# Revit family: Faucet-Two_Handle-American_Standard-Monterrey-6409180.002
name_source: partatom
category: Plumbing Fixtures
units: mm (PartAtom-declared; Revit-internal decimal feet)

## family parameters
Always vertical = No
Cut with Voids When Loaded = No
OmniClass Number = 23.45.55.17
OmniClass Title = Mixing Faucets
Part Type = Normal
Room Calculation Point = No
Round Connector Dimension = Use Diameter
Shared = Yes
Work Plane-Based = Yes

## types (1)
- 6409180.002
    ADA Compliant = Yes
    Assembly Code = D2020300
    CW Connection = Yes
    CWFU = 1.5
    CalGreen Compliant = Yes
    Cold Water Connection Diameter = 1/2"
    Compliance Certifications = These products meet or exceed the following codes and standards: ASME A112.18.1, CSA B125.1
NSF 61/Section 9, Annex G
CALGreen
    Default Elevation = 0"
    Description = Monterrey® Top Mount Kitchen Faucet With Gooseneck Spout and Wrist Blade Handles 1.5 gpm/5.7 Lpf Laminar Flow in Spout Base
    Finish = Brass-American Standard-002-Polished Chrome
    Flow Rate = 1.5gpm (5.7L/min)
    HW Connection = Yes
    HWFU = 1.5
    Height = 13 3/8"
    Hot Water Connection Diameter = 1/2"
    Installation Type = Deck Mounted
    L10 1.0 gpm (3.8 Lpm) PCA Non-Aerated Laminar Flow Outlet = No
    Length = 8"
    Manufacturer = American Standard
    Material = Brass-American Standard-002-Polished Chrome
    Model = 6409180.002
    Product Documentation Link = https://americanstandard.box.com
    Product Page URL = https://www.americanstandard-us.com
    Revised Date = 09/23/2022
    URL = http://www.americanstandard-us.com
    Vent Connection = No
    WFU = 2
    Waste Connection = No
    Width = 15 3/4"

## geometry (parser evidence)
native form markers: Sweep x2
no freeform markers — native parametric forms only
